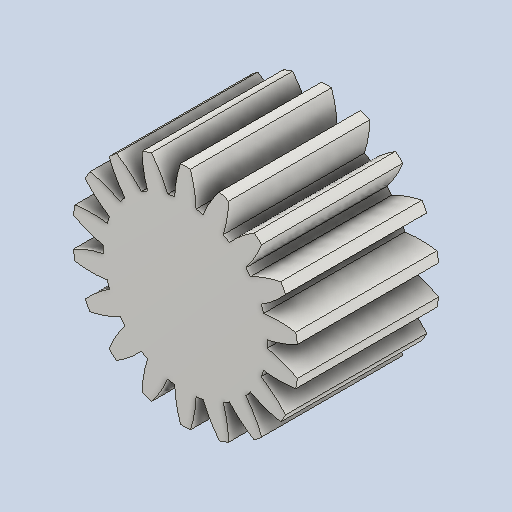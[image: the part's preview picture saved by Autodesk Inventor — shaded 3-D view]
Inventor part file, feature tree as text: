
AUTODESK INVENTOR PART (.ipt)
format: ipt  version: 2023.1 (Build 271208000, 208)  size: 253,952 bytes
history: native  units: mm (DEFAULTED — no unit token found)
features: plane x3, other x3, sketch x2, extrude x1
ambient origin geometry x8: Origin, YZ Plane, XZ Plane, XY Plane, X Axis, Y Axis, Z Axis, Center Point
bodies: Solid1 (feature_tree)
feature tree (9):
  extrude  "Extrusion1"  Depth=20.0mm TaperAngle=0.0deg
  plane  "Work Plane2"
  plane  "Work Plane8"
  plane  "Work Plane9"
  other  "Spur Gear"
  sketch  "Sketch1"  dims[d0=32.0mm d1=20.0mm d2=0.0mm]
  sketch  "Sketch2"  dims[d3=26.0mm d4=10.0mm d5=0.0mm d16=30.0mm d17=0.0mm d34=1.745329mm d39=0.0mm d41=0.0mm d43=30.0mm d46=30.0mm d47=0.0mm d48=0.0mm]
  other  "Srf1"
  other  "Pitch Diameter"
